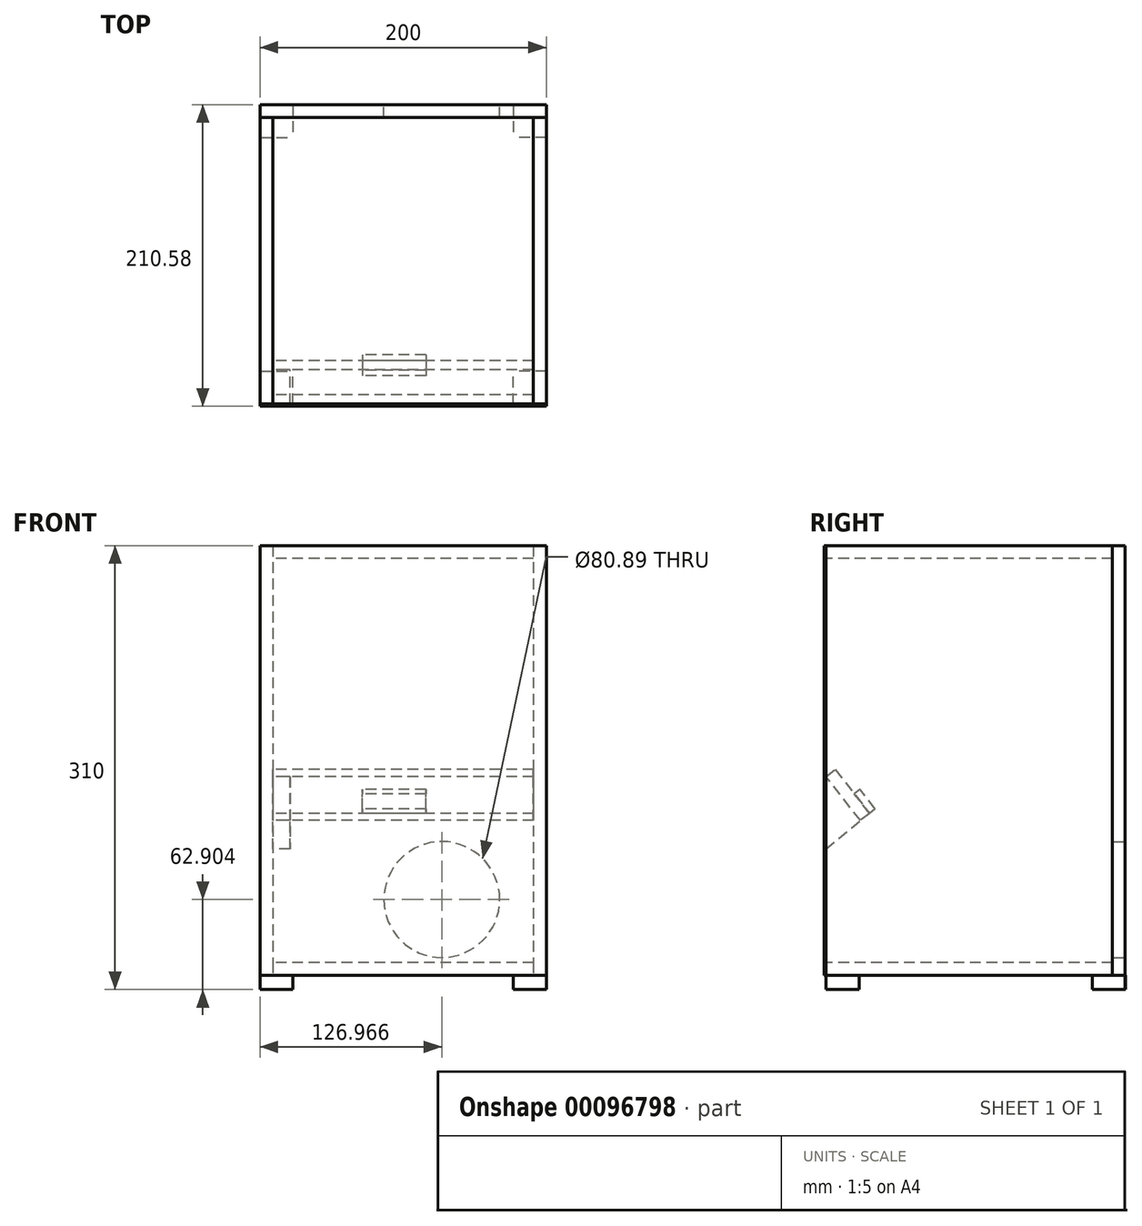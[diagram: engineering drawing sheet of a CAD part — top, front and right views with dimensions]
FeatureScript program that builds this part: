
annotation { "Feature Type Name" : "Feature", "Feature Type Description" : "" }
export const myFeature = defineFeature(function(context is Context, id is Id, definition is map)
    precondition{}
    {
        {
            var Q0;
            Q0=qCreatedBy(makeId("Front.planeOp"),FACE);
            var sketch = newSketch(context, id + "F0", { "sketchPlane" : qUnion([Q0])});
            skLineSegment(sketch, "E0.bottom", {"start": v(0, 0) * mm, "end": v(200, 0) * mm});
            skLineSegment(sketch, "E0.top", {"start": v(0, 300) * mm, "end": v(200, 300) * mm});
            skLineSegment(sketch, "E0.left", {"start": v(0, 0) * mm, "end": v(0, 300) * mm});
            skLineSegment(sketch, "E0.right", {"start": v(200, 0) * mm, "end": v(200, 300) * mm});
            skSolve(sketch);
        }
        {
            var Q0;
            Q0 = qSketchRegion(id + "F0", true);
            extrude(context, id + "F1", {"entities" : qUnion([Q0]), "depth" : 1.5 * mm});
        }
        {
            var Q0;
            Q0=makeQuery(id+"F1.opExtrude","CAP_FACE",FACE,{"disambiguationData":[OSD([sQuery(id+"F0.wireOp",EDGE,"E0.bottom"),sQuery(id+"F0.wireOp",EDGE,"E0.top"),sQuery(id+"F0.wireOp",EDGE,"E0.left"),sQuery(id+"F0.wireOp",EDGE,"E0.right")])],"isStart":true});
            var sketch = newSketch(context, id + "F2", { "sketchPlane" : qUnion([Q0])});
            skLineSegment(sketch, "E1.bottom", {"start": v(0, 300) * mm, "end": v(-9, 300) * mm});
            skLineSegment(sketch, "E1.top", {"start": v(0, 0) * mm, "end": v(-9, 0) * mm});
            skLineSegment(sketch, "E1.left", {"start": v(0, 300) * mm, "end": v(0, 0) * mm});
            skLineSegment(sketch, "E1.right", {"start": v(-9, 300) * mm, "end": v(-9, 0) * mm});
            skSolve(sketch);
        }
        {
            var Q0;
            Q0 = qSketchRegion(id + "F2", true);
            extrude(context, id + "F3", {"entities" : qUnion([Q0]), "depth" : 200 * mm});
        }
        {
            var Q0;
            Q0=makeQuery(id+"F3.opExtrude","SWEPT_FACE",FACE,{"disambiguationData":[OSD([sQuery(id+"F2.wireOp",EDGE,"E1.right")])]});
            var sketch = newSketch(context, id + "F4", { "sketchPlane" : qUnion([Q0])});
            skLineSegment(sketch, "E2", {"start": v(0, 138.7) * mm, "end": v(0, 88.15) * mm});
            skLineSegment(sketch, "E3", {"start": v(0, 88.15) * mm, "end": v(24, 108.1) * mm});
            skLineSegment(sketch, "E4", {"start": v(24, 108.1) * mm, "end": v(0, 138.7) * mm});
            skSolve(sketch);
        }
        {
            var Q0;
            Q0 = qSketchRegion(id + "F4", true);
            extrude(context, id + "F5", {"entities" : qUnion([Q0]), "depth" : 12 * mm});
        }
        {
            var Q0;
            Q0=makeQuery(id+"F3.opExtrude","SWEPT_FACE",FACE,{"disambiguationData":[OSD([sQuery(id+"F2.wireOp",EDGE,"E1.right")])]});
            var sketch = newSketch(context, id + "F6", { "sketchPlane" : qUnion([Q0])});
            skLineSegment(sketch, "E5", {"start": v(24, 108.1) * mm, "end": v(0, 138.7) * mm});
            skLineSegment(sketch, "E6", {"start": v(0, 138.7) * mm, "end": v(6.36, 143.69) * mm});
            skLineSegment(sketch, "E7", {"start": v(6.36, 143.69) * mm, "end": v(30.36, 113.08) * mm});
            skLineSegment(sketch, "E8", {"start": v(30.36, 113.08) * mm, "end": v(24, 108.1) * mm});
            skSolve(sketch);
        }
        {
            var Q0;
            Q0 = qSketchRegion(id + "F6", true);
            extrude(context, id + "F7", {"entities" : qUnion([Q0]), "depth" : 182 * mm});
        }
        {
            var Q0;
            Q0=makeQuery(id+"F7.opExtrude","SWEPT_FACE",FACE,{"disambiguationData":[OSD([sQuery(id+"F6.wireOp",EDGE,"E7")])]});
            var sketch = newSketch(context, id + "F8", { "sketchPlane" : qUnion([Q0])});
            skLineSegment(sketch, "E9.bottom", {"start": v(-115.8, 70.24) * mm, "end": v(-71.6, 70.24) * mm});
            skLineSegment(sketch, "E9.top", {"start": v(-115.8, 87.47) * mm, "end": v(-71.6, 87.47) * mm});
            skLineSegment(sketch, "E9.left", {"start": v(-115.8, 70.24) * mm, "end": v(-115.8, 87.47) * mm});
            skLineSegment(sketch, "E9.right", {"start": v(-71.6, 70.24) * mm, "end": v(-71.6, 87.47) * mm});
            skSolve(sketch);
        }
        {
            var Q0;
            Q0 = qSketchRegion(id + "F8", true);
            extrude(context, id + "F9", {"entities" : qUnion([Q0]), "depth" : 5 * mm});
        }
        {
            var Q0;
            Q0=makeQuery(id+"F3.opExtrude","SWEPT_FACE",FACE,{"disambiguationData":[OSD([sQuery(id+"F2.wireOp",EDGE,"E1.right")])]});
            var sketch = newSketch(context, id + "F10", { "sketchPlane" : qUnion([Q0])});
            skLineSegment(sketch, "E10.bottom", {"start": v(200, 300) * mm, "end": v(0, 300) * mm});
            skLineSegment(sketch, "E10.top", {"start": v(200, 291) * mm, "end": v(0, 291) * mm});
            skLineSegment(sketch, "E10.left", {"start": v(200, 300) * mm, "end": v(200, 291) * mm});
            skLineSegment(sketch, "E10.right", {"start": v(0, 300) * mm, "end": v(0, 291) * mm});
            skSolve(sketch);
        }
        {
            var Q0;
            Q0 = qSketchRegion(id + "F10", true);
            extrude(context, id + "F11", {"entities" : qUnion([Q0]), "depth" : 182 * mm});
        }
        {
            var Q0;
            Q0=makeQuery(id+"F3.opExtrude","SWEPT_FACE",FACE,{"disambiguationData":[OSD([sQuery(id+"F2.wireOp",EDGE,"E1.right")])]});
            var sketch = newSketch(context, id + "F12", { "sketchPlane" : qUnion([Q0])});
            skLineSegment(sketch, "E11.bottom", {"start": v(200, 0) * mm, "end": v(0, 0) * mm});
            skLineSegment(sketch, "E11.top", {"start": v(200, 9) * mm, "end": v(0, 9) * mm});
            skLineSegment(sketch, "E11.left", {"start": v(200, 0) * mm, "end": v(200, 9) * mm});
            skLineSegment(sketch, "E11.right", {"start": v(0, 0) * mm, "end": v(0, 9) * mm});
            skSolve(sketch);
        }
        {
            var Q0;
            Q0 = qSketchRegion(id + "F12", true);
            extrude(context, id + "F13", {"entities" : qUnion([Q0]), "depth" : 182 * mm});
        }
        {
            var Q0;
            Q0=makeQuery(id+"F11.opExtrude","CAP_FACE",FACE,{"disambiguationData":[OSD([sQuery(id+"F10.wireOp",EDGE,"E10.bottom"),sQuery(id+"F10.wireOp",EDGE,"E10.top"),sQuery(id+"F10.wireOp",EDGE,"E10.left"),sQuery(id+"F10.wireOp",EDGE,"E10.right")])],"isStart":false});
            var sketch = newSketch(context, id + "F14", { "sketchPlane" : qUnion([Q0])});
            skLineSegment(sketch, "E12.bottom", {"start": v(200, 300) * mm, "end": v(0, 300) * mm});
            skLineSegment(sketch, "E12.top", {"start": v(200, 0) * mm, "end": v(0, 0) * mm});
            skLineSegment(sketch, "E12.left", {"start": v(200, 300) * mm, "end": v(200, 0) * mm});
            skLineSegment(sketch, "E12.right", {"start": v(0, 300) * mm, "end": v(0, 0) * mm});
            skSolve(sketch);
        }
        {
            var Q0;
            Q0 = qSketchRegion(id + "F14", true);
            extrude(context, id + "F15", {"entities" : qUnion([Q0]), "depth" : 9 * mm});
        }
        {
            var Q0;
            Q0=makeQuery(id+"F15.opExtrude","SWEPT_FACE",FACE,{"disambiguationData":[OSD([sQuery(id+"F14.wireOp",EDGE,"E12.left")])]});
            var sketch = newSketch(context, id + "F16", { "sketchPlane" : qUnion([Q0])});
            skLineSegment(sketch, "E13.bottom", {"start": v(-200, 300) * mm, "end": v(0, 300) * mm});
            skLineSegment(sketch, "E13.top", {"start": v(-200, 0) * mm, "end": v(0, 0) * mm});
            skLineSegment(sketch, "E13.left", {"start": v(-200, 300) * mm, "end": v(-200, 0) * mm});
            skLineSegment(sketch, "E13.right", {"start": v(0, 300) * mm, "end": v(0, 0) * mm});
            skSolve(sketch);
        }
        {
            var Q0;
            Q0 = qSketchRegion(id + "F16", true);
            extrude(context, id + "F17", {"entities" : qUnion([Q0]), "depth" : 9 * mm});
        }
        {
            var Q0;
            Q0=makeQuery(id+"F17.opExtrude","CAP_FACE",FACE,{"disambiguationData":[OSD([sQuery(id+"F16.wireOp",EDGE,"E13.bottom"),sQuery(id+"F16.wireOp",EDGE,"E13.top"),sQuery(id+"F16.wireOp",EDGE,"E13.left"),sQuery(id+"F16.wireOp",EDGE,"E13.right")])],"isStart":false});
            var sketch = newSketch(context, id + "F18", { "sketchPlane" : qUnion([Q0])});
            skCircle(sketch, "E14", {"center": v(-126.97, 52.9) * mm, "radius": 40.44 * mm});
            skSolve(sketch);
        }
        {
            var Q0;
            Q0 = qSketchRegion(id + "F18", true);
            extrude(context, id + "F19", {"entities" : qUnion([Q0]), "operationType" : NewBodyOperationType.REMOVE, "oppositeDirection" : true, "depth" : 9 * mm});
        }
        {
            var Q0;
            Q0=makeQuery(id+"F13.opExtrude","SWEPT_FACE",FACE,{"disambiguationData":[OSD([sQuery(id+"F12.wireOp",EDGE,"E11.bottom")])]});
            var sketch = newSketch(context, id + "F20", { "sketchPlane" : qUnion([Q0])});
            skLineSegment(sketch, "E15.bottom", {"start": v(0, 0) * mm, "end": v(23, 0) * mm});
            skLineSegment(sketch, "E15.top", {"start": v(0, -23) * mm, "end": v(23, -23) * mm});
            skLineSegment(sketch, "E15.left", {"start": v(0, 0) * mm, "end": v(0, -23) * mm});
            skLineSegment(sketch, "E15.right", {"start": v(23, 0) * mm, "end": v(23, -23) * mm});
            skSolve(sketch);
        }
        {
            var Q0;
            Q0 = qSketchRegion(id + "F20", true);
            extrude(context, id + "F21", {"entities" : qUnion([Q0]), "depth" : 10 * mm});
        }
        {
            var Q0;
            Q0=makeQuery(id+"F13.opExtrude","SWEPT_FACE",FACE,{"disambiguationData":[OSD([sQuery(id+"F12.wireOp",EDGE,"E11.bottom")])]});
            var sketch = newSketch(context, id + "F22", { "sketchPlane" : qUnion([Q0])});
            skLineSegment(sketch, "E16.bottom", {"start": v(200, 0) * mm, "end": v(177, 0) * mm});
            skLineSegment(sketch, "E16.top", {"start": v(200, -23) * mm, "end": v(177, -23) * mm});
            skLineSegment(sketch, "E16.left", {"start": v(200, 0) * mm, "end": v(200, -23) * mm});
            skLineSegment(sketch, "E16.right", {"start": v(177, 0) * mm, "end": v(177, -23) * mm});
            skSolve(sketch);
        }
        {
            var Q0;
            Q0 = qSketchRegion(id + "F22", true);
            extrude(context, id + "F23", {"entities" : qUnion([Q0]), "depth" : 10 * mm});
        }
        {
            var Q0;
            Q0=makeQuery(id+"F13.opExtrude","SWEPT_FACE",FACE,{"disambiguationData":[OSD([sQuery(id+"F12.wireOp",EDGE,"E11.bottom")])]});
            var sketch = newSketch(context, id + "F24", { "sketchPlane" : qUnion([Q0])});
            skLineSegment(sketch, "E17.bottom", {"start": v(0, -209.08) * mm, "end": v(23, -209.08) * mm});
            skLineSegment(sketch, "E17.top", {"start": v(0, -186.08) * mm, "end": v(23, -186.08) * mm});
            skLineSegment(sketch, "E17.left", {"start": v(0, -209.08) * mm, "end": v(0, -186.08) * mm});
            skLineSegment(sketch, "E17.right", {"start": v(23, -209.08) * mm, "end": v(23, -186.08) * mm});
            skSolve(sketch);
        }
        {
            var Q0;
            Q0 = qSketchRegion(id + "F24", true);
            extrude(context, id + "F25", {"entities" : qUnion([Q0]), "depth" : 10 * mm});
        }
        {
            var Q0;
            Q0=makeQuery(id+"F13.opExtrude","SWEPT_FACE",FACE,{"disambiguationData":[OSD([sQuery(id+"F12.wireOp",EDGE,"E11.bottom")])]});
            var sketch = newSketch(context, id + "F26", { "sketchPlane" : qUnion([Q0])});
            skLineSegment(sketch, "E18.bottom", {"start": v(200, -209) * mm, "end": v(177, -209) * mm});
            skLineSegment(sketch, "E18.top", {"start": v(200, -186) * mm, "end": v(177, -186) * mm});
            skLineSegment(sketch, "E18.left", {"start": v(200, -209) * mm, "end": v(200, -186) * mm});
            skLineSegment(sketch, "E18.right", {"start": v(177, -209) * mm, "end": v(177, -186) * mm});
            skSolve(sketch);
        }
        {
            var Q0;
            Q0 = qSketchRegion(id + "F26", true);
            extrude(context, id + "F27", {"entities" : qUnion([Q0]), "depth" : 10 * mm});
        }
    });
